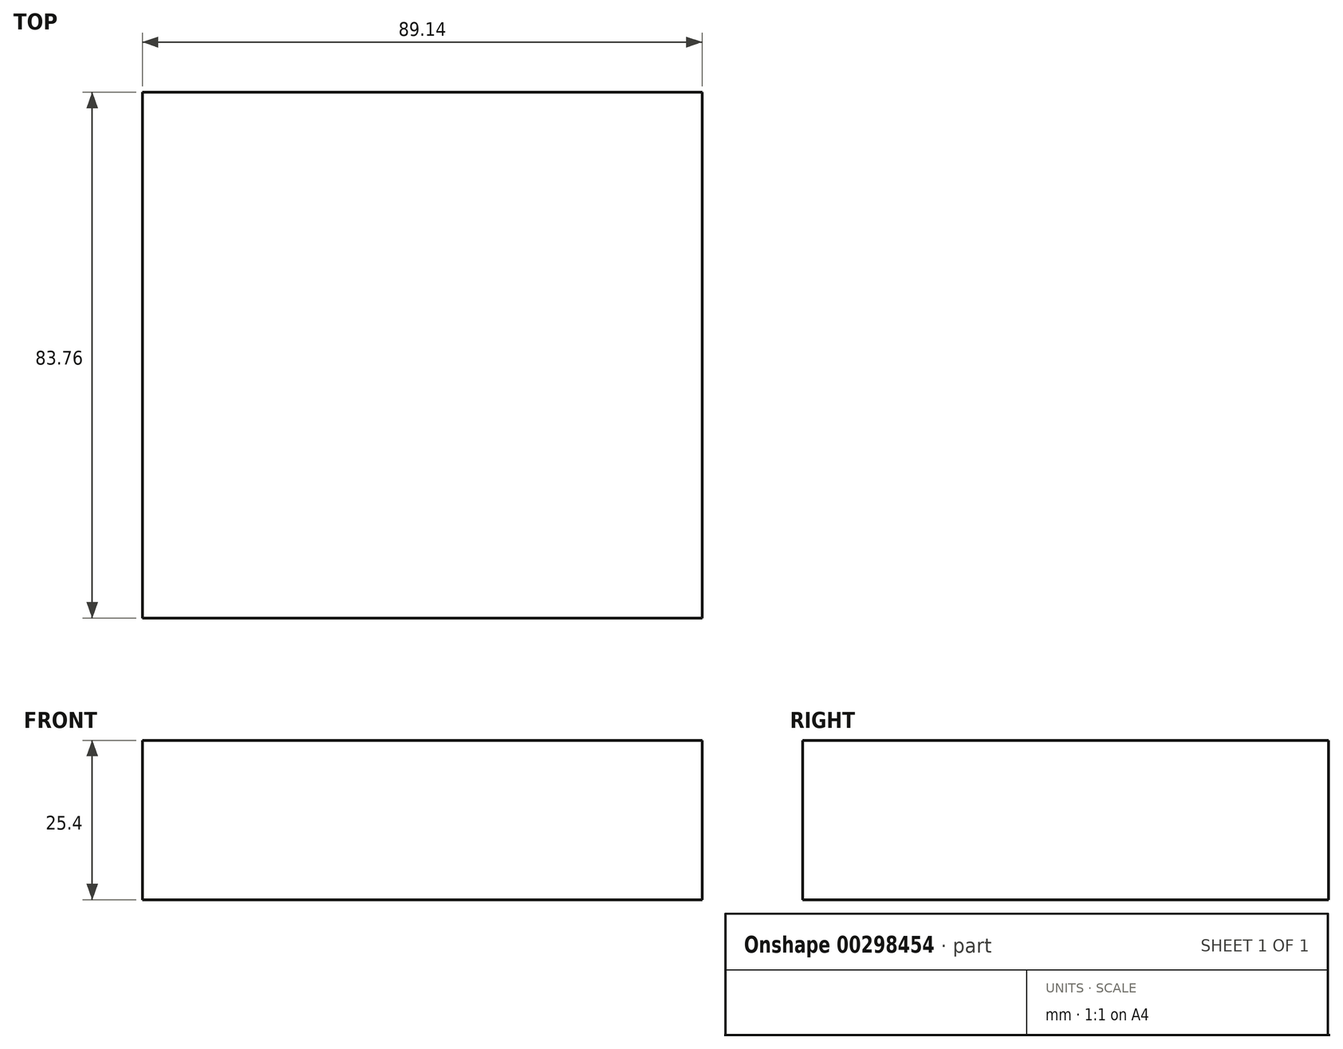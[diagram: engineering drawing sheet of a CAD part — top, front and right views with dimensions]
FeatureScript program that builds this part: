
annotation { "Feature Type Name" : "Feature", "Feature Type Description" : "" }
export const myFeature = defineFeature(function(context is Context, id is Id, definition is map)
    precondition{}
    {
        {
            var Q0;
            Q0=qCreatedBy(makeId("Top.planeOp"),FACE);
            var sketch = newSketch(context, id + "F0", { "sketchPlane" : qUnion([Q0])});
            skLineSegment(sketch, "E0.bottom", {"start": v(44.57, 41.88) * mm, "end": v(-44.57, 41.88) * mm});
            skLineSegment(sketch, "E0.top", {"start": v(44.57, -41.88) * mm, "end": v(-44.57, -41.88) * mm});
            skLineSegment(sketch, "E0.left", {"start": v(44.57, 41.88) * mm, "end": v(44.57, -41.88) * mm});
            skLineSegment(sketch, "E0.right", {"start": v(-44.57, 41.88) * mm, "end": v(-44.57, -41.88) * mm});
            skPoint(sketch, "E0.middle", {"position": v(0, 0) * mm});
            skSolve(sketch);
        }
        {
            var Q0;
            Q0 = qSketchRegion(id + "F0", true);
            extrude(context, id + "F1", {"entities" : qUnion([Q0]), "depth" : 25.4 * mm});
        }
    });
